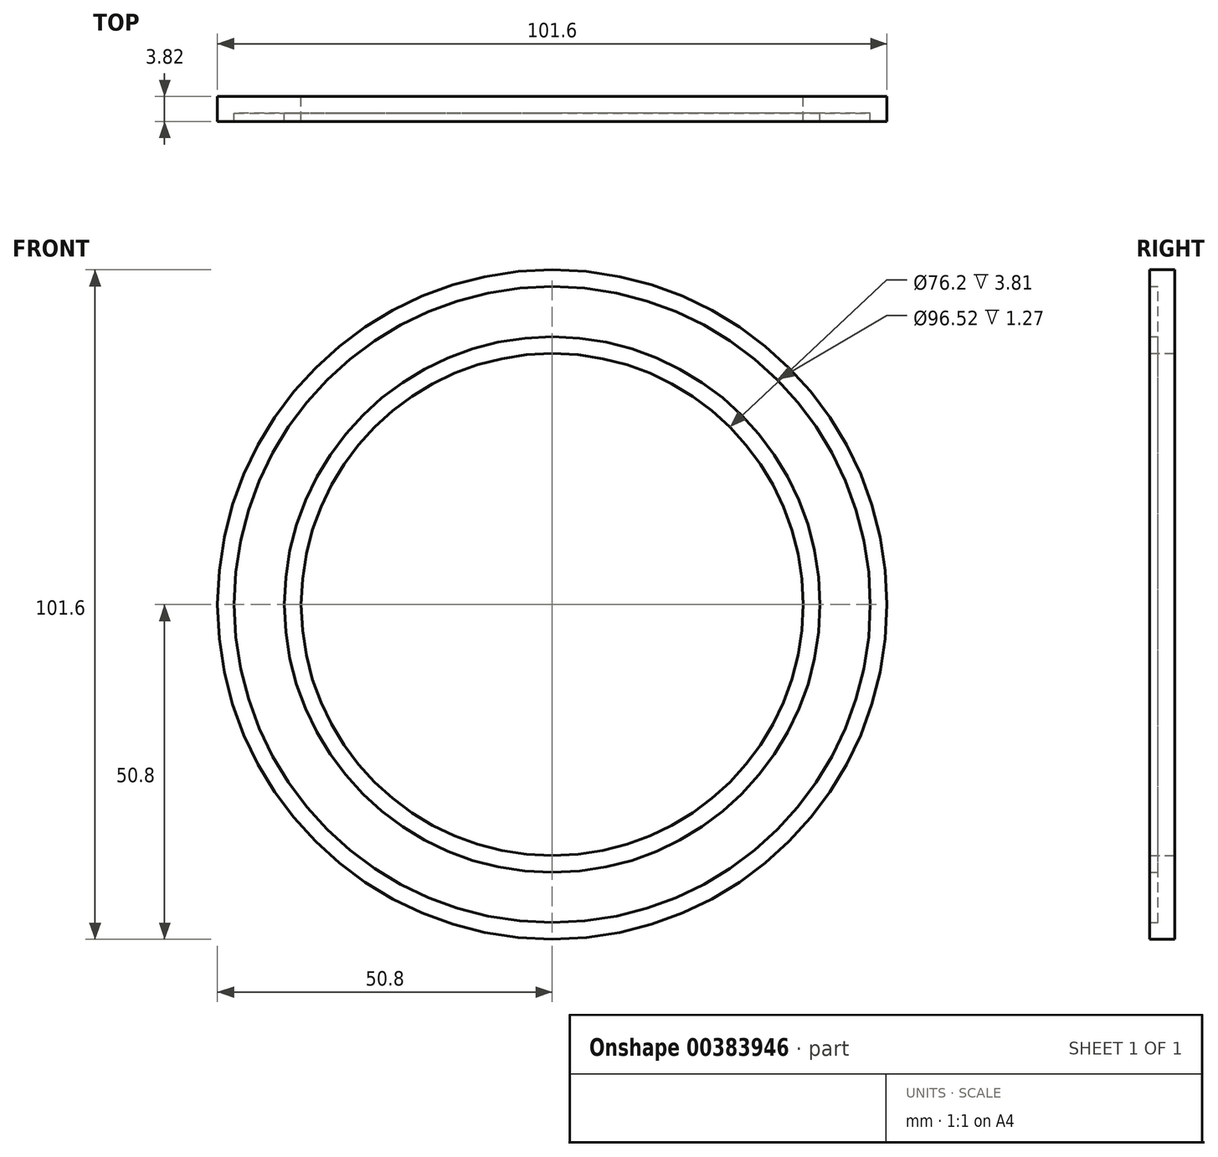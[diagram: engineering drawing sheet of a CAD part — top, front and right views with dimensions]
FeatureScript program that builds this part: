
annotation { "Feature Type Name" : "Feature", "Feature Type Description" : "" }
export const myFeature = defineFeature(function(context is Context, id is Id, definition is map)
    precondition{}
    {
        {
            var Q0;
            Q0=qCreatedBy(makeId("Front.planeOp"),FACE);
            var sketch = newSketch(context, id + "F0", { "sketchPlane" : qUnion([Q0])});
            skCircle(sketch, "E0", {"center": v(0, 0) * mm, "radius": 50.8 * mm});
            skCircle(sketch, "E1", {"center": v(0, 0) * mm, "radius": 38.1 * mm});
            skSolve(sketch);
        }
        {
            var Q0;
            Q0=makeQuery(id+"F0.imprint","IMPRINT",FACE,{"disambiguationData":[TD([[makeQuery(id+"F0.imprint","IMPRINT",EDGE,{"derivedFrom":sQuery(id+"F0.wireOp",EDGE,"E0")}),1.0]])]});
            extrude(context, id + "F1", {"entities" : qUnion([Q0]), "endBound" : BoundingType.SYMMETRIC, "depth" : 3.8 * mm});
        }
        {
            var Q0;
            Q0=makeQuery(id+"F1.opExtrude","CAP_FACE",FACE,{"disambiguationData":[OSD([sQuery(id+"F0.wireOp",EDGE,"E0"),sQuery(id+"F0.wireOp",EDGE,"E1")])],"isStart":false});
            shell(context, id + "F2", {"entities" : qUnion([Q0]), "thickness" : 2.54 * mm});
        }
    });
